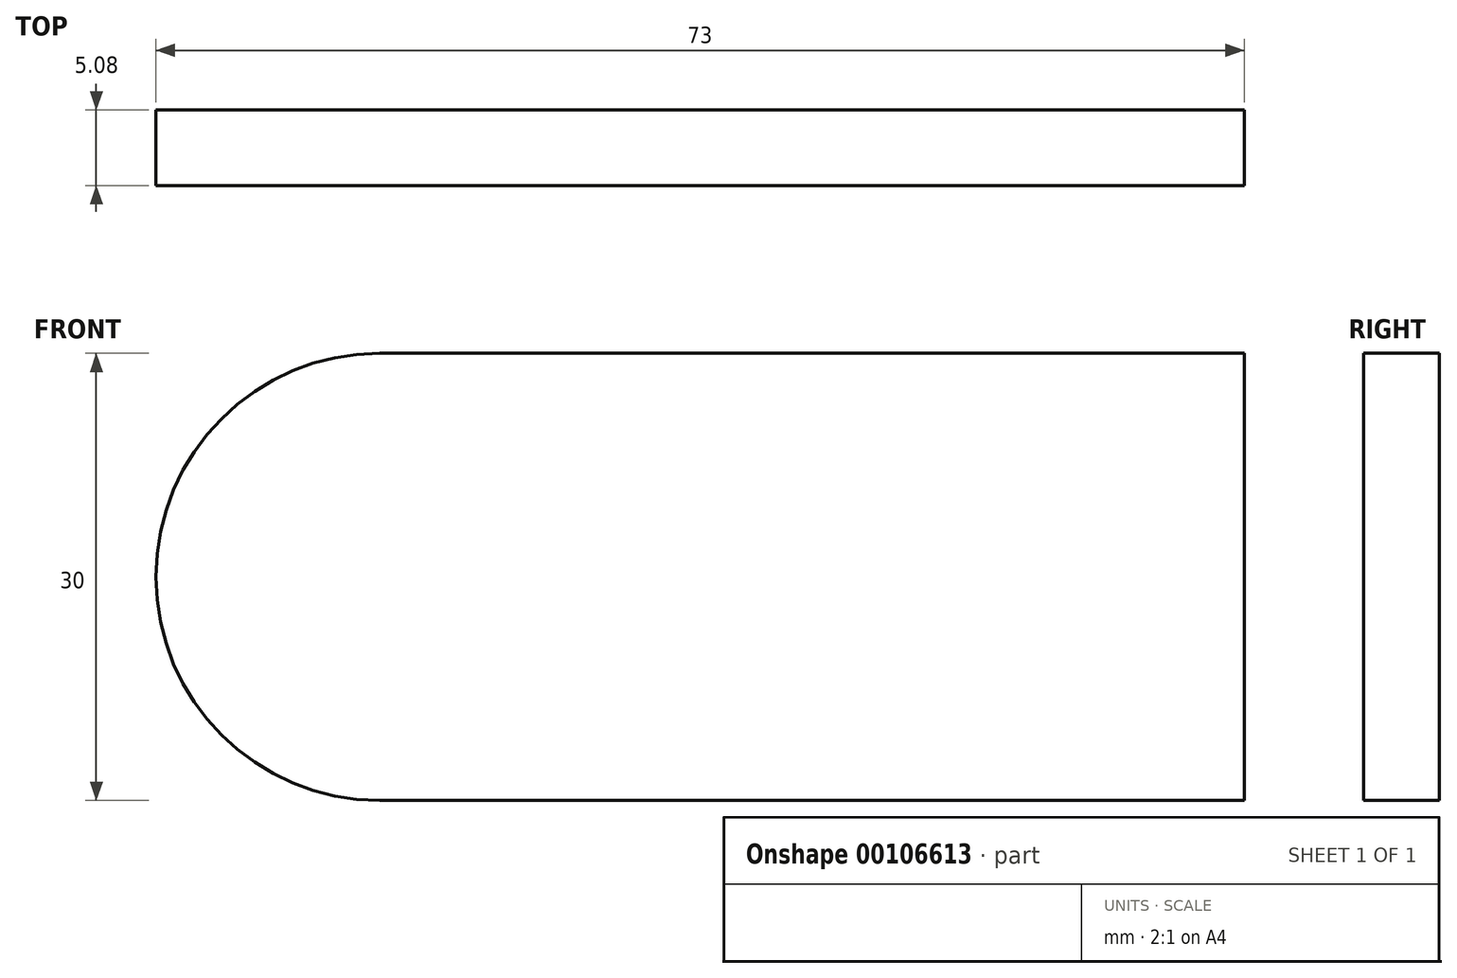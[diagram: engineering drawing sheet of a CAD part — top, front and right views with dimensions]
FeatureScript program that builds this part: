
annotation { "Feature Type Name" : "Feature", "Feature Type Description" : "" }
export const myFeature = defineFeature(function(context is Context, id is Id, definition is map)
    precondition{}
    {
        {
            var Q0;
            Q0=qCreatedBy(makeId("Front.planeOp"),FACE);
            var sketch = newSketch(context, id + "F0", { "sketchPlane" : qUnion([Q0])});
            skLineSegment(sketch, "E0.bottom", {"start": v(-152.51, 7.05) * mm, "end": v(-94.51, 7.05) * mm});
            skLineSegment(sketch, "E0.top", {"start": v(-152.51, 37.05) * mm, "end": v(-94.51, 37.05) * mm});
            skLineSegment(sketch, "E0.right", {"start": v(-94.51, 7.05) * mm, "end": v(-94.51, 37.05) * mm});
            skArc(sketch, "E1", {"start": v(-152.51, 37.05) * mm, "mid": v(-167.51, 22.05) * mm, "end": v(-152.51, 7.05) * mm});
            skSolve(sketch);
        }
        {
            var Q0;
            Q0=makeQuery(id+"F0.imprint","IMPRINT",FACE,{"disambiguationData":[TD([[makeQuery(id+"F0.imprint","IMPRINT",EDGE,{"derivedFrom":sQuery(id+"F0.wireOp",EDGE,"E0.bottom")}),1.0]])]});
            extrude(context, id + "F1", {"entities" : qUnion([Q0]), "oppositeDirection" : true, "depth" : 5.08 * mm});
        }
    });
